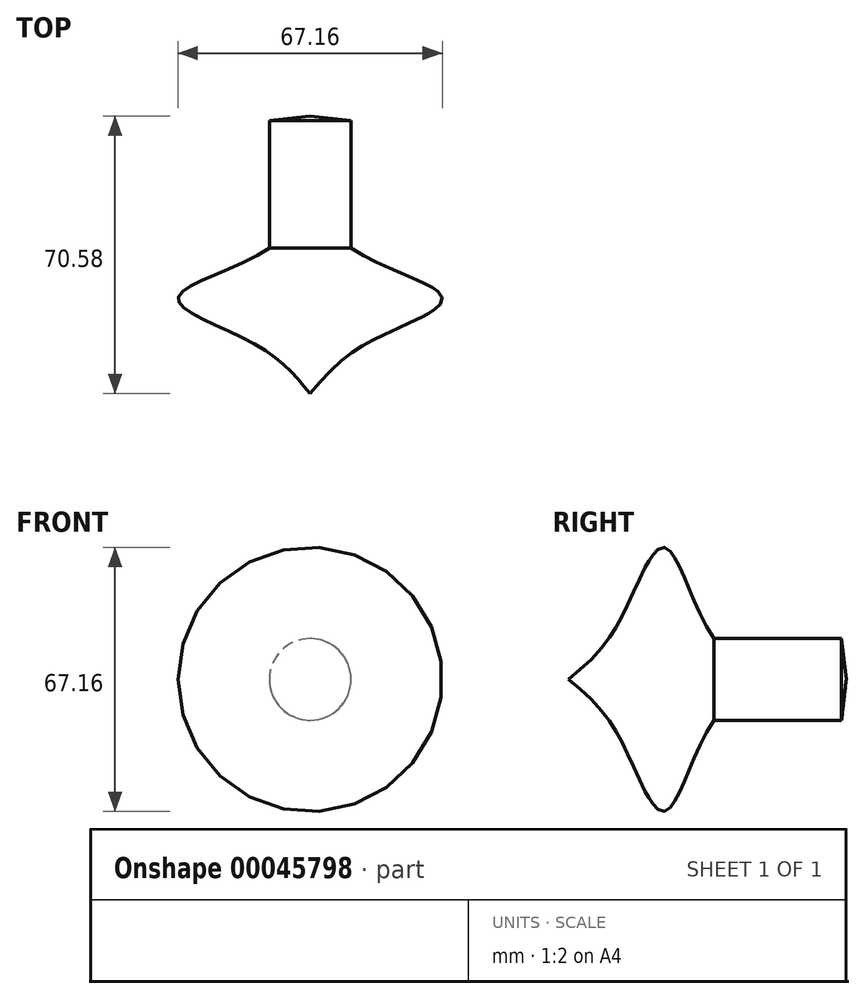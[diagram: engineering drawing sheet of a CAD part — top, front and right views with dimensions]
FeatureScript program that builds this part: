
annotation { "Feature Type Name" : "Feature", "Feature Type Description" : "" }
export const myFeature = defineFeature(function(context is Context, id is Id, definition is map)
    precondition{}
    {
        {
            var Q0;
            Q0=qCreatedBy(makeId("Top.planeOp"),FACE);
            var sketch = newSketch(context, id + "F0", { "sketchPlane" : qUnion([Q0])});
            skFitSpline(sketch, "E0", {"points": [v(0, 31.14) * mm, v(-10.38, 12.82) * mm, v(-33.58, 0) * mm, v(-14.45, -11.4) * mm, v(0, -24.22) * mm], "startDerivative": vector(-20.2, -82.17) * mm, "endDerivative": vector(46.8, -57.03) * mm});
            skLineSegment(sketch, "E1", {"start": v(0, 31.14) * mm, "end": v(0, -24.22) * mm});
            skFitSpline(sketch, "E2", {"points": [v(-10.38, 12.82) * mm, v(-4.45, 40.54) * mm, v(0, 46.36) * mm], "startDerivative": vector(7.52, 49.95) * mm, "endDerivative": vector(13.93, 13.14) * mm});
            skLineSegment(sketch, "E3", {"start": v(0, 46.36) * mm, "end": v(0, 31.14) * mm});
            skLineSegment(sketch, "E4", {"start": v(-10.38, 12.82) * mm, "end": v(-10.38, 45.21) * mm});
            skLineSegment(sketch, "E5", {"start": v(-10.38, 45.21) * mm, "end": v(0, 46.36) * mm});
            skLineSegment(sketch, "E6", {"start": v(-10.38, 29.02) * mm, "end": v(-5.19, 45.79) * mm});
            skSolve(sketch);
        }
        {
            var Q0;
            Q0 = qSketchRegion(id + "F0", true);
            var Q1;
            Q1=sQuery(id+"F0.wireOp",EDGE,"E1");
            revolve(context, id + "F1", {"entities" : qUnion([Q0]), "axis" : qUnion([Q1]), "revolveType" : RevolveType.FULL});
        }
    });
